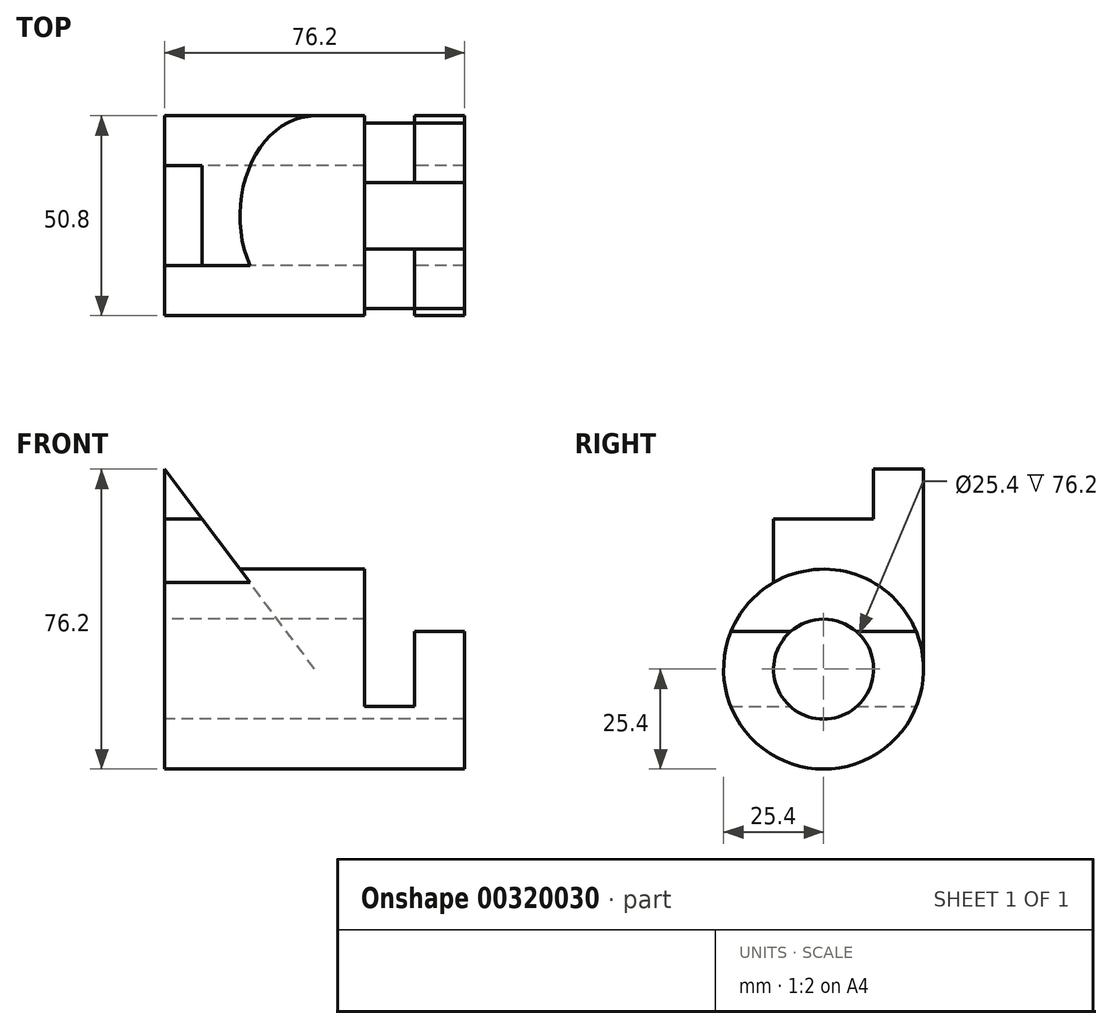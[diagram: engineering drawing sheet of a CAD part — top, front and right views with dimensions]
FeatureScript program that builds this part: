
annotation { "Feature Type Name" : "Feature", "Feature Type Description" : "" }
export const myFeature = defineFeature(function(context is Context, id is Id, definition is map)
    precondition{}
    {
        {
            var Q0;
            Q0=qCreatedBy(makeId("Right.planeOp"),FACE);
            var sketch = newSketch(context, id + "F0", { "sketchPlane" : qUnion([Q0])});
            skCircle(sketch, "E0", {"center": v(0, 0) * mm, "radius": 25.4 * mm});
            skSolve(sketch);
        }
        {
            var Q0;
            Q0 = qSketchRegion(id + "F0", true);
            extrude(context, id + "F1", {"entities" : qUnion([Q0]), "endBound" : BoundingType.SYMMETRIC, "depth" : 50.8 * mm});
        }
        {
            var Q0;
            Q0=makeQuery(id+"F1.opExtrude","CAP_FACE",FACE,{"disambiguationData":[OSD([sQuery(id+"F0.wireOp",EDGE,"E0")])],"isStart":false});
            var sketch = newSketch(context, id + "F2", { "sketchPlane" : qUnion([Q0])});
            skCircle(sketch, "E1.0", {"center": v(0, 0) * mm, "radius": 25.4 * mm});
            skLineSegment(sketch, "E2", {"start": v(-23.55, 9.53) * mm, "end": v(-8.4, 9.53) * mm});
            skCircle(sketch, "E3", {"center": v(0, 0) * mm, "radius": 12.7 * mm});
            skLineSegment(sketch, "E4.trimOffspring", {"start": v(8.4, 9.53) * mm, "end": v(23.55, 9.53) * mm});
            skSolve(sketch);
        }
        {
            var Q0;
            {var subQ0=sQuery(id+"F2.wireOp",EDGE,"E2");Q0=makeQuery(id+"F2.imprint","IMPRINT",FACE,{"disambiguationData":[TD([[makeQuery(id+"F2.imprint","IMPRINT",EDGE,{"derivedFrom":subQ0}),-1.0]])]});}
            extrude(context, id + "F3", {"entities" : qUnion([Q0]), "operationType" : NewBodyOperationType.ADD, "depth" : 25.4 * mm});
        }
        {
            var Q0;
            Q0=makeQuery(id+"F1.opExtrude","CAP_FACE",FACE,{"disambiguationData":[OSD([sQuery(id+"F0.wireOp",EDGE,"E0")])],"isStart":false});
            var sketch = newSketch(context, id + "F4", { "sketchPlane" : qUnion([Q0])});
            skArc(sketch, "E5.0", {"start": v(23.55, -9.53) * mm, "mid": v(0, 25.4) * mm, "end": v(-23.55, -9.52) * mm});
            skLineSegment(sketch, "E6", {"start": v(-23.55, -9.52) * mm, "end": v(23.55, -9.52) * mm});
            skSolve(sketch);
        }
        {
            var Q0;
            Q0=makeQuery(id+"F4.imprint","IMPRINT",FACE,{"disambiguationData":[TD([[makeQuery(id+"F4.imprint","IMPRINT",EDGE,{"derivedFrom":sQuery(id+"F4.wireOp",EDGE,"E5.0")}),1.0]])]});
            extrude(context, id + "F5", {"entities" : qUnion([Q0]), "operationType" : NewBodyOperationType.REMOVE, "depth" : 12.7 * mm});
        }
        {
            var Q0;
            Q0=qCreatedBy(makeId("Front.planeOp"),FACE);
            var sketch = newSketch(context, id + "F6", { "sketchPlane" : qUnion([Q0])});
            skLineSegment(sketch, "E7.0", {"start": v(-25.4, 25.4) * mm, "end": v(-25.4, -25.4) * mm});
            skLineSegment(sketch, "E8", {"start": v(-25.4, 25.4) * mm, "end": v(25.4, 25.4) * mm});
            skLineSegment(sketch, "E9", {"start": v(12.7, 0) * mm, "end": v(-25.4, 50.8) * mm});
            skLineSegment(sketch, "E10", {"start": v(-25.4, 50.8) * mm, "end": v(-25.4, 0) * mm});
            skLineSegment(sketch, "E11", {"start": v(-25.4, 0) * mm, "end": v(12.7, 0) * mm});
            skSolve(sketch);
        }
        {
            var Q0;
            {var subQ5=sQuery(id+"F6.wireOp",EDGE,"E11");Q0=makeQuery(id+"F6.imprint","IMPRINT",FACE,{"disambiguationData":[TD([[makeQuery(id+"F6.imprint","IMPRINT",EDGE,{"derivedFrom":subQ5}),1.0]])]});}
            var Q1;
            {var subQ0=sQuery(id+"F6.wireOp",EDGE,"E10");var subQ1=sQuery(id+"F6.wireOp",EDGE,"E8");var subQ2=makeQuery(id+"F6.imprint","INTERSECT",VERTEX,{"derivedFrom":[subQ1,subQ0]});Q1=makeQuery(id+"F6.imprint","IMPRINT",FACE,{"disambiguationData":[TD([[makeQuery(id+"F6.imprint","IMPRINT",EDGE,{"disambiguationData":[TD([[subQ2,-1.0]])],"derivedFrom":subQ1}),1.0]])]});}
            extrude(context, id + "F7", {"entities" : qUnion([Q0, Q1]), "operationType" : NewBodyOperationType.ADD, "oppositeDirection" : true, "depth" : 25.4 * mm});
        }
        {
            var Q0;
            Q0 = qSketchRegion(id + "F6", true);
            extrude(context, id + "F8", {"entities" : qUnion([Q0]), "operationType" : NewBodyOperationType.ADD, "depth" : 12.7 * mm});
        }
        {
            var Q0;
            {var subQ0=sQuery(id+"F6.wireOp",EDGE,"E10");Q0=makeQuery(id+"F8.boolean.opBoolean","MERGE",FACE,{"derivedFrom":[makeQuery(id+"F7.boolean.opBoolean","MERGE",FACE,{"derivedFrom":[makeQuery(id+"F1.opExtrude","CAP_FACE",FACE,{"disambiguationData":[OSD([sQuery(id+"F0.wireOp",EDGE,"E0")])],"isStart":true}),makeQuery(id+"F7.opExtrude","SWEPT_FACE",FACE,{"disambiguationData":[OSD([subQ0])]})]}),makeQuery(id+"F8.opExtrude","SWEPT_FACE",FACE,{"disambiguationData":[OSD([subQ0])]})]});}
            var sketch = newSketch(context, id + "F9", { "sketchPlane" : qUnion([Q0])});
            skLineSegment(sketch, "E12.bottom", {"start": v(-12.7, 50.8) * mm, "end": v(12.7, 50.8) * mm});
            skLineSegment(sketch, "E12.top", {"start": v(-12.7, 38.1) * mm, "end": v(12.7, 38.1) * mm});
            skLineSegment(sketch, "E12.left", {"start": v(-12.7, 50.8) * mm, "end": v(-12.7, 38.1) * mm});
            skLineSegment(sketch, "E12.right", {"start": v(12.7, 50.8) * mm, "end": v(12.7, 38.1) * mm});
            skSolve(sketch);
        }
        {
            var Q0;
            Q0 = qSketchRegion(id + "F9", true);
            extrude(context, id + "F10", {"entities" : qUnion([Q0]), "operationType" : NewBodyOperationType.REMOVE, "endBound" : BoundingType.THROUGH_ALL, "oppositeDirection" : true, "depth" : 25.4 * mm});
        }
        {
            var Q0;
            {var subQ0=sQuery(id+"F2.wireOp",EDGE,"E3");var subQ1=makeQuery(id+"F2.imprint","INTERSECT",VERTEX,{"derivedFrom":[sQuery(id+"F2.wireOp",EDGE,"E2"),subQ0]});Q0=makeQuery(id+"F2.imprint","IMPRINT",FACE,{"disambiguationData":[TD([[makeQuery(id+"F2.imprint","IMPRINT",EDGE,{"disambiguationData":[TD([[subQ1,1.0]])],"derivedFrom":subQ0}),1.0]])]});}
            extrude(context, id + "F11", {"entities" : qUnion([Q0]), "operationType" : NewBodyOperationType.REMOVE, "endBound" : BoundingType.THROUGH_ALL, "oppositeDirection" : true, "depth" : 25.4 * mm});
        }
    });
